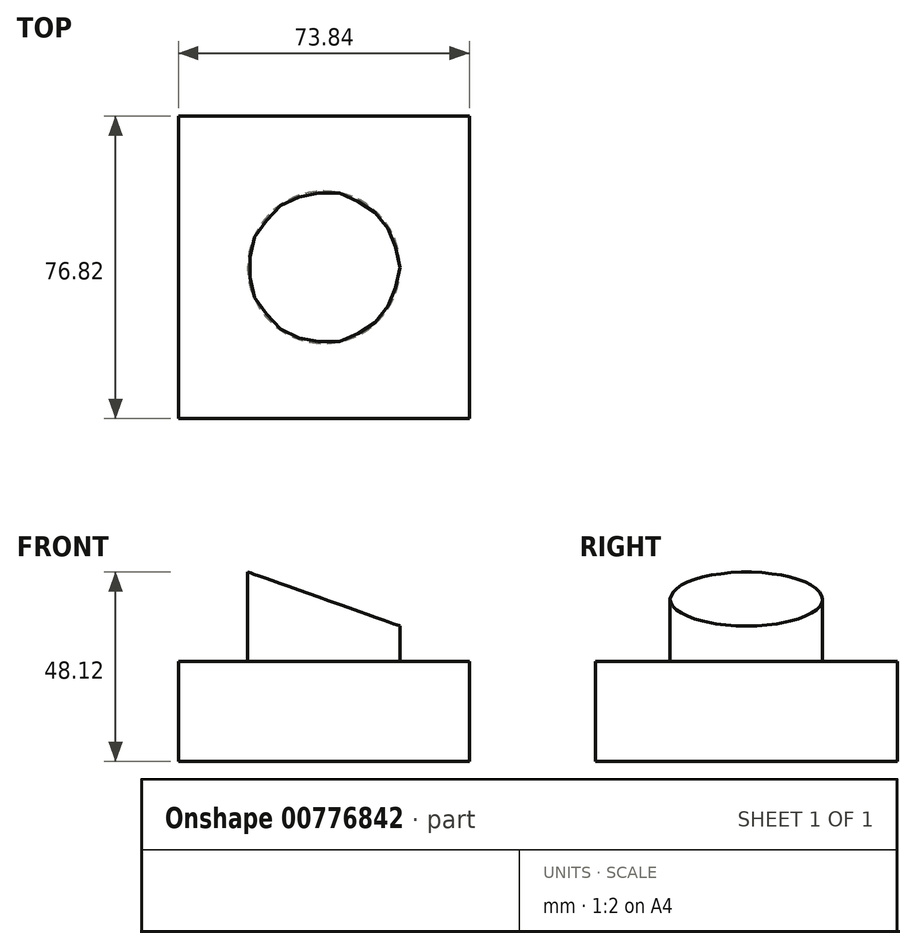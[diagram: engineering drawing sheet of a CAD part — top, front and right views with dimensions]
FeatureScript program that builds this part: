
annotation { "Feature Type Name" : "Feature", "Feature Type Description" : "" }
export const myFeature = defineFeature(function(context is Context, id is Id, definition is map)
    precondition{}
    {
        {
            var Q0;
            Q0=qCreatedBy(makeId("Top.planeOp"),FACE);
            var sketch = newSketch(context, id + "F0", { "sketchPlane" : qUnion([Q0])});
            skLineSegment(sketch, "E0.bottom", {"start": v(36.92, 38.4) * mm, "end": v(-36.92, 38.4) * mm});
            skLineSegment(sketch, "E0.top", {"start": v(36.92, -38.4) * mm, "end": v(-36.92, -38.4) * mm});
            skLineSegment(sketch, "E0.left", {"start": v(36.92, 38.4) * mm, "end": v(36.92, -38.4) * mm});
            skLineSegment(sketch, "E0.right", {"start": v(-36.92, 38.4) * mm, "end": v(-36.92, -38.4) * mm});
            skPoint(sketch, "E0.middle", {"position": v(0, 0) * mm});
            skSolve(sketch);
        }
        {
            var Q0;
            Q0=makeQuery(id+"F0.imprint","IMPRINT",FACE,{"disambiguationData":[TD([[makeQuery(id+"F0.imprint","IMPRINT",EDGE,{"derivedFrom":sQuery(id+"F0.wireOp",EDGE,"E0.bottom")}),1.0]])]});
            extrude(context, id + "F1", {"entities" : qUnion([Q0]), "depth" : 25.4 * mm, "offsetDistance" : 25.4 * mm});
        }
        {
            var Q0;
            Q0=makeQuery(id+"F1.opExtrude","CAP_FACE",FACE,{"disambiguationData":[OSD([sQuery(id+"F0.wireOp",EDGE,"E0.bottom"),sQuery(id+"F0.wireOp",EDGE,"E0.top"),sQuery(id+"F0.wireOp",EDGE,"E0.left"),sQuery(id+"F0.wireOp",EDGE,"E0.right")])],"isStart":false});
            var sketch = newSketch(context, id + "F2", { "sketchPlane" : qUnion([Q0])});
            skCircle(sketch, "E1", {"center": v(0, 0) * mm, "radius": 19.36 * mm});
            skSolve(sketch);
        }
        {
            var Q0;
            Q0=makeQuery(id+"F2.imprint","IMPRINT",FACE,{"disambiguationData":[TD([[makeQuery(id+"F2.imprint","IMPRINT",EDGE,{"derivedFrom":sQuery(id+"F2.wireOp",EDGE,"E1")}),1.0]])]});
            extrude(context, id + "F3", {"entities" : qUnion([Q0]), "operationType" : NewBodyOperationType.ADD, "depth" : 25.4 * mm, "offsetDistance" : 25.4 * mm});
        }
        {
            var Q0;
            Q0=qCreatedBy(makeId("Front.planeOp"),FACE);
            var sketch = newSketch(context, id + "F4", { "sketchPlane" : qUnion([Q0])});
            skLineSegment(sketch, "E2", {"start": v(-42.33, 56.26) * mm, "end": v(49.76, 23.62) * mm});
            skLineSegment(sketch, "E3", {"start": v(-42.33, 56.26) * mm, "end": v(20.83, 68.2) * mm});
            skLineSegment(sketch, "E4", {"start": v(20.83, 68.2) * mm, "end": v(49.76, 23.62) * mm});
            skSolve(sketch);
        }
        {
            var Q0;
            Q0=makeQuery(id+"F4.imprint","IMPRINT",FACE,{"disambiguationData":[TD([[makeQuery(id+"F4.imprint","IMPRINT",EDGE,{"derivedFrom":sQuery(id+"F4.wireOp",EDGE,"E2")}),1.0]])]});
            extrude(context, id + "F5", {"entities" : qUnion([Q0]), "operationType" : NewBodyOperationType.REMOVE, "endBound" : BoundingType.SYMMETRIC, "oppositeDirection" : true, "depth" : 50.8 * mm, "offsetDistance" : 25.4 * mm});
        }
    });
